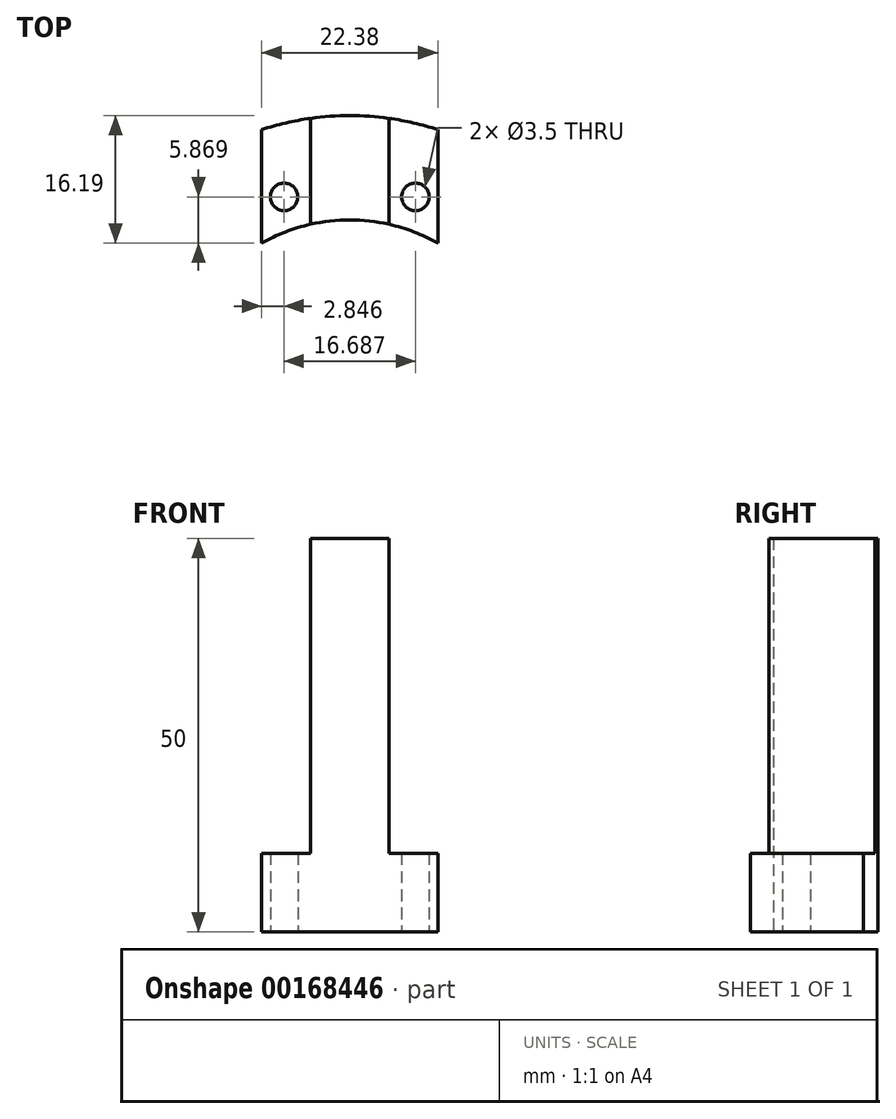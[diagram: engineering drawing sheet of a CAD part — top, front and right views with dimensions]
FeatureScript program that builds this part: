
annotation { "Feature Type Name" : "Feature", "Feature Type Description" : "" }
export const myFeature = defineFeature(function(context is Context, id is Id, definition is map)
    precondition{}
    {
        {
            var Q0;
            Q0=qCreatedBy(makeId("Top.planeOp"),FACE);
            var sketch = newSketch(context, id + "F0", { "sketchPlane" : qUnion([Q0])});
            skCircle(sketch, "E0", {"center": v(0, 0) * mm, "radius": 22.75 * mm});
            skCircle(sketch, "E1", {"center": v(0, 0) * mm, "radius": 36 * mm});
            skCircle(sketch, "E2", {"center": v(0, 0) * mm, "radius": 27 * mm});
            skCircle(sketch, "E3", {"center": v(-27, 0) * mm, "radius": 1.75 * mm});
            skCircle(sketch, "E4.1.0", {"center": v(-21.84, -15.87) * mm, "radius": 1.75 * mm});
            skCircle(sketch, "E4.2.0", {"center": v(-8.34, -25.68) * mm, "radius": 1.75 * mm});
            skCircle(sketch, "E4.3.0", {"center": v(8.34, -25.68) * mm, "radius": 1.75 * mm});
            skCircle(sketch, "E4.4.0", {"center": v(21.84, -15.87) * mm, "radius": 1.75 * mm});
            skCircle(sketch, "E4.5.0", {"center": v(27, 0) * mm, "radius": 1.75 * mm});
            skCircle(sketch, "E4.6.0", {"center": v(21.84, 15.87) * mm, "radius": 1.75 * mm});
            skCircle(sketch, "E4.7.0", {"center": v(8.34, 25.68) * mm, "radius": 1.75 * mm});
            skCircle(sketch, "E4.8.0", {"center": v(-8.34, 25.68) * mm, "radius": 1.75 * mm});
            skCircle(sketch, "E4.9.0", {"center": v(-21.84, 15.87) * mm, "radius": 1.75 * mm});
            skLineSegment(sketch, "E5", {"start": v(-4.99, 35.65) * mm, "end": v(-4.99, 22.2) * mm});
            skLineSegment(sketch, "E6", {"start": v(-11.2, 19.8) * mm, "end": v(-11.2, 34.22) * mm});
            skLineSegment(sketch, "E7.MirrorCS", {"start": v(4.99, 35.65) * mm, "end": v(4.99, 22.2) * mm});
            skLineSegment(sketch, "E8.MirrorCS", {"start": v(11.2, 19.8) * mm, "end": v(11.2, 34.22) * mm});
            skSolve(sketch);
        }
        {
            var Q0;
            {var subQ3=sQuery(id+"F0.wireOp",EDGE,"E5");var subQ8=sQuery(id+"F0.wireOp",EDGE,"E1");var subQ9=makeQuery(id+"F0.imprint","INTERSECT",VERTEX,{"derivedFrom":[subQ8,subQ3]});Q0=makeQuery(id+"F0.imprint","IMPRINT",FACE,{"disambiguationData":[TD([[makeQuery(id+"F0.imprint","IMPRINT",EDGE,{"disambiguationData":[TD([[subQ9,-1.0]])],"derivedFrom":subQ8}),1.0]])]});}
            var Q1;
            {var subQ0=sQuery(id+"F0.wireOp",EDGE,"E5");var subQ1=sQuery(id+"F0.wireOp",EDGE,"E1");var subQ2=makeQuery(id+"F0.imprint","INTERSECT",VERTEX,{"derivedFrom":[subQ1,subQ0]});Q1=makeQuery(id+"F0.imprint","IMPRINT",FACE,{"disambiguationData":[TD([[makeQuery(id+"F0.imprint","IMPRINT",EDGE,{"disambiguationData":[TD([[subQ2,1.0]])],"derivedFrom":subQ1}),1.0]])]});}
            var Q2;
            {var subQ3=sQuery(id+"F0.wireOp",EDGE,"E7.MirrorCS");var subQ8=sQuery(id+"F0.wireOp",EDGE,"E1");var subQ9=makeQuery(id+"F0.imprint","INTERSECT",VERTEX,{"derivedFrom":[subQ8,subQ3]});Q2=makeQuery(id+"F0.imprint","IMPRINT",FACE,{"disambiguationData":[TD([[makeQuery(id+"F0.imprint","IMPRINT",EDGE,{"disambiguationData":[TD([[subQ9,1.0]])],"derivedFrom":subQ8}),1.0]])]});}
            var Q3;
            {var subQ5=sQuery(id+"F0.wireOp",EDGE,"E7.MirrorCS");var subQ6=sQuery(id+"F0.wireOp",EDGE,"E0");var subQ7=makeQuery(id+"F0.imprint","INTERSECT",VERTEX,{"derivedFrom":[subQ6,subQ5]});Q3=makeQuery(id+"F0.imprint","IMPRINT",FACE,{"disambiguationData":[TD([[makeQuery(id+"F0.imprint","IMPRINT",EDGE,{"disambiguationData":[TD([[subQ7,1.0]])],"derivedFrom":subQ6}),-1.0]])]});}
            var Q4;
            {var subQ6=sQuery(id+"F0.wireOp",EDGE,"E5");var subQ8=sQuery(id+"F0.wireOp",EDGE,"E0");var subQ9=makeQuery(id+"F0.imprint","INTERSECT",VERTEX,{"derivedFrom":[subQ8,subQ6]});Q4=makeQuery(id+"F0.imprint","IMPRINT",FACE,{"disambiguationData":[TD([[makeQuery(id+"F0.imprint","IMPRINT",EDGE,{"disambiguationData":[TD([[subQ9,-1.0]])],"derivedFrom":subQ8}),-1.0]])]});}
            var Q5;
            {var subQ0=sQuery(id+"F0.wireOp",EDGE,"E5");var subQ1=sQuery(id+"F0.wireOp",EDGE,"E0");var subQ2=makeQuery(id+"F0.imprint","INTERSECT",VERTEX,{"derivedFrom":[subQ1,subQ0]});Q5=makeQuery(id+"F0.imprint","IMPRINT",FACE,{"disambiguationData":[TD([[makeQuery(id+"F0.imprint","IMPRINT",EDGE,{"disambiguationData":[TD([[subQ2,1.0]])],"derivedFrom":subQ1}),-1.0]])]});}
            extrude(context, id + "F1", {"entities" : qUnion([Q0, Q1, Q2, Q3, Q4, Q5]), "depth" : 10 * mm, "offsetDistance" : 25 * mm});
        }
        {
            var Q0;
            {var subQ0=sQuery(id+"F0.wireOp",EDGE,"E5");var subQ1=sQuery(id+"F0.wireOp",EDGE,"E1");var subQ2=makeQuery(id+"F0.imprint","INTERSECT",VERTEX,{"derivedFrom":[subQ1,subQ0]});Q0=makeQuery(id+"F0.imprint","IMPRINT",FACE,{"disambiguationData":[TD([[makeQuery(id+"F0.imprint","IMPRINT",EDGE,{"disambiguationData":[TD([[subQ2,1.0]])],"derivedFrom":subQ1}),1.0]])]});}
            var Q1;
            {var subQ0=sQuery(id+"F0.wireOp",EDGE,"E5");var subQ1=sQuery(id+"F0.wireOp",EDGE,"E0");var subQ2=makeQuery(id+"F0.imprint","INTERSECT",VERTEX,{"derivedFrom":[subQ1,subQ0]});Q1=makeQuery(id+"F0.imprint","IMPRINT",FACE,{"disambiguationData":[TD([[makeQuery(id+"F0.imprint","IMPRINT",EDGE,{"disambiguationData":[TD([[subQ2,1.0]])],"derivedFrom":subQ1}),-1.0]])]});}
            extrude(context, id + "F2", {"entities" : qUnion([Q0, Q1]), "operationType" : NewBodyOperationType.ADD, "depth" : 50 * mm, "offsetDistance" : 25 * mm});
        }
    });
